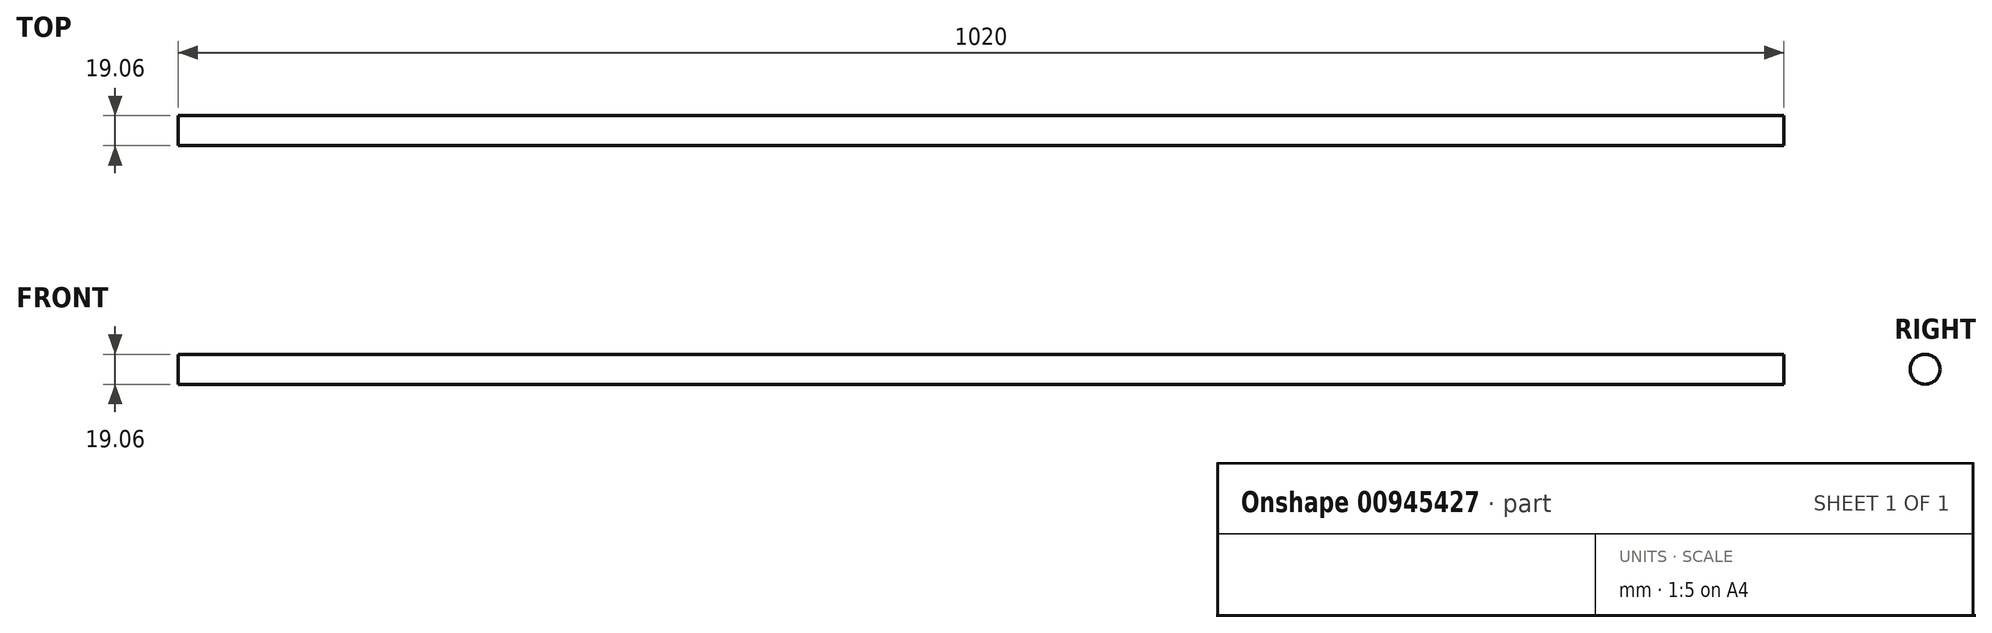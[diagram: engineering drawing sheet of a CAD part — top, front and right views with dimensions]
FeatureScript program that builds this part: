
annotation { "Feature Type Name" : "Feature", "Feature Type Description" : "" }
export const myFeature = defineFeature(function(context is Context, id is Id, definition is map)
    precondition{}
    {
        {
            var Q0;
            Q0=qCreatedBy(makeId("Right.planeOp"),FACE);
            var sketch = newSketch(context, id + "F0", { "sketchPlane" : qUnion([Q0])});
            skCircle(sketch, "E0", {"center": v(0, 0) * mm, "radius": 9.53 * mm});
            skSolve(sketch);
        }
        {
            var Q0;
            Q0=sQuery(id+"F0.wireOp",EDGE,"E0");
            extrude(context, id + "F1", {"bodyType" : ToolBodyType.SURFACE, "surfaceEntities" : qUnion([Q0]), "depth" : 1020 * mm, "offsetDistance" : 25.4 * mm});
        }
    });
